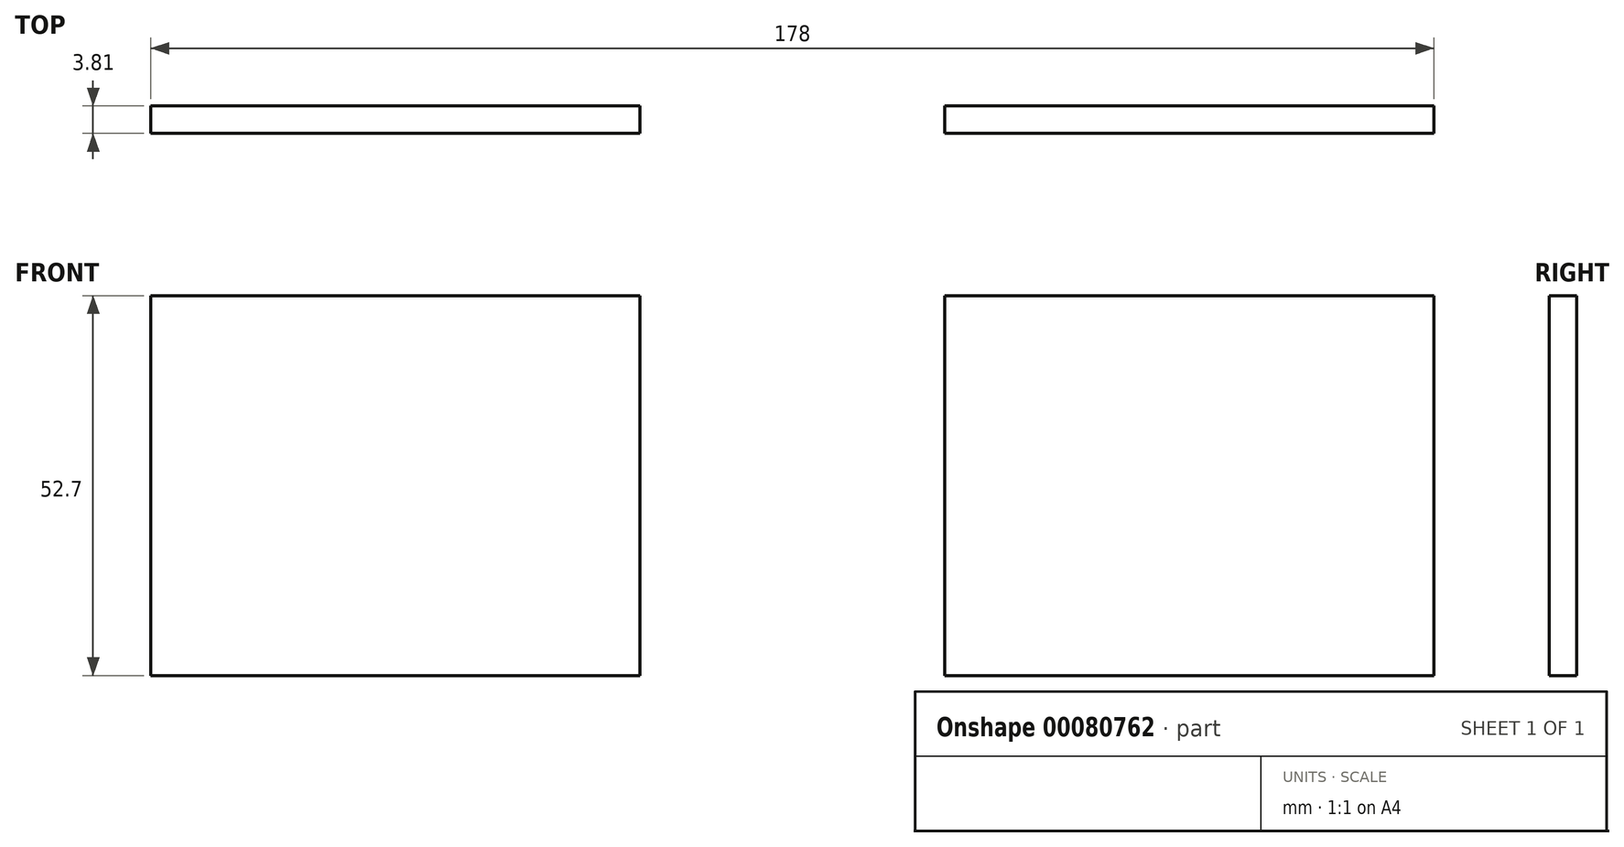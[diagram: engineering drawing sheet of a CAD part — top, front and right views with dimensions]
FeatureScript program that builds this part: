
annotation { "Feature Type Name" : "Feature", "Feature Type Description" : "" }
export const myFeature = defineFeature(function(context is Context, id is Id, definition is map)
    precondition{}
    {
        {
            var Q0;
            Q0=qCreatedBy(makeId("Front.planeOp"),FACE);
            var sketch = newSketch(context, id + "F0", { "sketchPlane" : qUnion([Q0])});
            skLineSegment(sketch, "E0.bottom", {"start": v(89, 26.35) * mm, "end": v(-89, 26.35) * mm});
            skLineSegment(sketch, "E0.top", {"start": v(89, -26.35) * mm, "end": v(-89, -26.35) * mm});
            skLineSegment(sketch, "E0.left", {"start": v(89, 26.35) * mm, "end": v(89, -26.35) * mm});
            skLineSegment(sketch, "E0.right", {"start": v(-89, 26.35) * mm, "end": v(-89, -26.35) * mm});
            skPoint(sketch, "E0.middle", {"position": v(0, 0) * mm});
            skLineSegment(sketch, "E1.bottom", {"start": v(21.14, 26.35) * mm, "end": v(-21.14, 26.35) * mm});
            skLineSegment(sketch, "E1.top", {"start": v(21.14, -26.35) * mm, "end": v(-21.14, -26.35) * mm});
            skLineSegment(sketch, "E1.left", {"start": v(21.14, 26.35) * mm, "end": v(21.14, -26.35) * mm});
            skLineSegment(sketch, "E1.right", {"start": v(-21.14, 26.35) * mm, "end": v(-21.14, -26.35) * mm});
            skSolve(sketch);
        }
        {
            var Q0;
            {var subQ0=sQuery(id+"F0.wireOp",EDGE,"E0.right");Q0=makeQuery(id+"F0.imprint","IMPRINT",FACE,{"disambiguationData":[TD([[makeQuery(id+"F0.imprint","IMPRINT",EDGE,{"derivedFrom":subQ0}),1.0]])]});}
            var Q1;
            {var subQ0=sQuery(id+"F0.wireOp",EDGE,"E0.left");Q1=makeQuery(id+"F0.imprint","IMPRINT",FACE,{"disambiguationData":[TD([[makeQuery(id+"F0.imprint","IMPRINT",EDGE,{"derivedFrom":subQ0}),-1.0]])]});}
            extrude(context, id + "F1", {"entities" : qUnion([Q0, Q1]), "depth" : 3.8 * mm});
        }
    });
